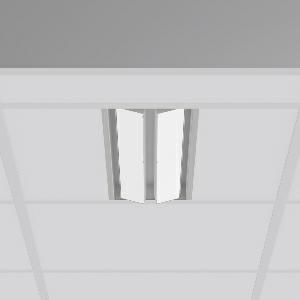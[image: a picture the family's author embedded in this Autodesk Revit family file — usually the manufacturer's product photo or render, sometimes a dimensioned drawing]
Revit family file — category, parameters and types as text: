
# Revit family: tx-move_901735_004_1_76_27e5
name_source: partatom
category: Lighting Fixtures
units: mm (PartAtom-declared; Revit-internal decimal feet)

## family parameters
Cut with Voids When Loaded = No
Host = Face
Light Source = No
Part Type = Normal
Room Calculation Point = No
Round Connector Dimension = Use Diameter
Shared = No

## types (1)
- MultiLumen 1 (1 x LED Modul 840, 2450 lm, 4000)
    Apparent Load = 35 VA
    Approval mark = CE
    CIE Flux Codes = 47 79 96 100 100
    Color Rendering = 80
    Color Temperature = 4000
    Default Elevation = 1800 mm
    Description = Series: TX-MOVE
Einlege/Einbau-Flächenstrahler. Housing: sheet steel, powder-coated. 2xSwivel range: 90°. High-efficiency LED units with flush-mounted opal diffuser made of non-yellowing PMMA. Symmetrical wide beam light emission. Suitable for laying in grid ceiling module 600. Connected converter included in separate gearbox.Suitable for through-wiring.MultiLumen: Luminous flux adjustable in 3 steps. Accessories: Mounting frame for installation in suspended ceilings. Environmentally friendly and resource-saving due to replaceable and recyclable components. 
Colour: silver, matt (approx. RAL 9006)
Length: 597 mm
Width: 190 mm
Height: 39 mm
Cut-out length: 577.5 mm
Cut-out width: 174 mm
Recess height: 100 mm
Lamp: LED
Socket: without socket
Colour temperature: 4000K
Colour rendering index (CRI): 80
System power: 35 W
Rated luminous flux: 4900 lm
Luminous efficiency: 140 lm/W
System power 2: 47 W
Rated luminous flux 2: 6450 lm
Luminous efficiency 2: 137 lm/W
System power 3: 68 W
Rated luminous flux 3: 8750 lm
Luminous efficiency 3: 129 lm/W
Control gear: Dimmable EVG, DALI
Protection class: I
Type of protection: IP 20
    Height = 0 mm  [stored 0 ft]
    Lamp = 1 x LED Modul 840
    Lamp Light Flux = 2450 lm
    Lamp count = 1
    Length = 597 mm
    Lifetime = 50000 h
    Luminous efficacy = 140 lm/W
    Manufacturer = RZB
    ModVariant = No
    Model = 901735.004.1.76
    Mounting Place = Ceiling, Wall
    Mounting Type = Recessed
    Number of Poles = 1
    OnlyDefault = Yes
    Power Factor = 1
    Product Name = TX-MOVE
    Product group = Recessed projectors
    ProductGroupID = 401
    Protection Class = Protection class I
    Protection Degree = IP 20
    RLX_Detail_Level = 1
    RLX_Emergency_Light_Flux = 0 lm
    RLX_Emergency_Type = 0
    RLX_Emergency_Type_DB = No
    RlxData = <blob elided: 31017 chars, md5=b46ce787>
    Socket = socket
    Standby Power = 0 W
    System Light Flux = 4900 lm
    System Power = 35 W
    Type Comments = MultiLumen 1
    Type Image = 901735.004.jpg
    URL = http://relux.com
    VarID = multilumen_1
    Voltage = 230 V
    Voltage Range = 220-240 V
    Weight = 0.00 kg
    Width = 190 mm  [stored 0.62336 ft]

note: [stored X ft] marks values corroborated as IEEE doubles in the binary element streams (Revit-internal decimal feet)

## geometry (parser evidence)
native form markers: Blend x4, Sweep x15
no freeform markers — native parametric forms only
